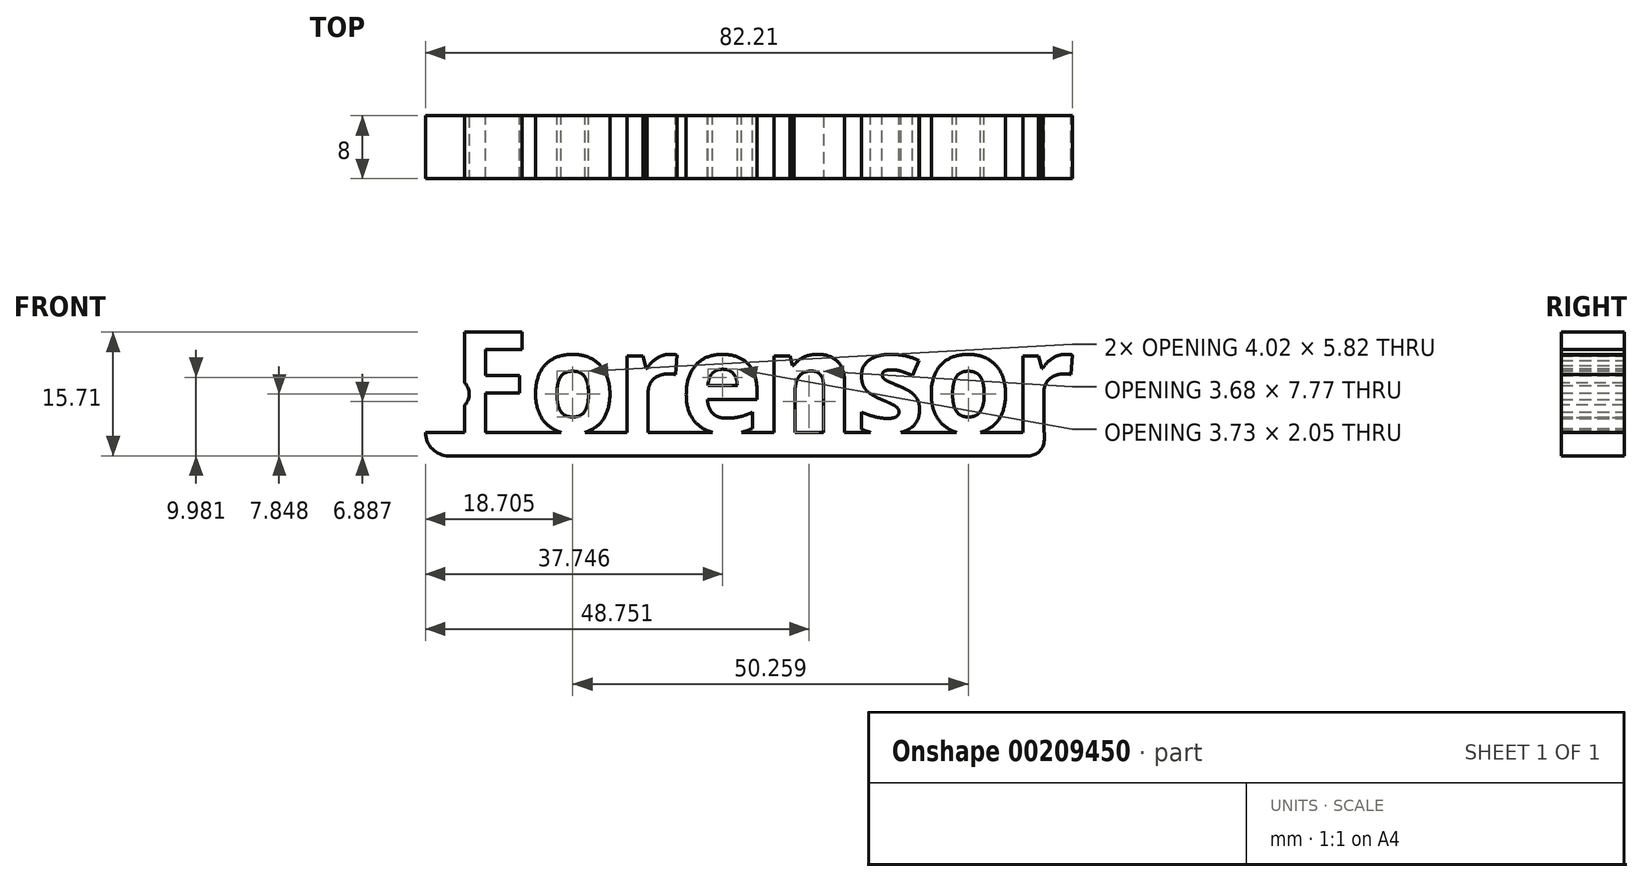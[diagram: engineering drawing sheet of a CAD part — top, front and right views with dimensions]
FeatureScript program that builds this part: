
annotation { "Feature Type Name" : "Feature", "Feature Type Description" : "" }
export const myFeature = defineFeature(function(context is Context, id is Id, definition is map)
    precondition{}
    {
        {
            var Q0;
            Q0=qCreatedBy(makeId("Top.planeOp"),FACE);
            var sketch = newSketch(context, id + "F0", { "sketchPlane" : qUnion([Q0])});
            skLineSegment(sketch, "E0.bottom", {"start": v(36.8, -4) * mm, "end": v(-36.8, -4) * mm});
            skLineSegment(sketch, "E0.top", {"start": v(36.8, 4) * mm, "end": v(-36.8, 4) * mm});
            skLineSegment(sketch, "E0.left", {"start": v(36.8, -4) * mm, "end": v(36.8, 4) * mm});
            skLineSegment(sketch, "E0.right", {"start": v(-36.8, -4) * mm, "end": v(-36.8, 4) * mm});
            skPoint(sketch, "E0.middle", {"position": v(0, 0) * mm});
            skSolve(sketch);
        }
        {
            var Q0;
            Q0=makeQuery(id+"F0.imprint","IMPRINT",FACE,{"disambiguationData":[TD([[makeQuery(id+"F0.imprint","IMPRINT",EDGE,{"derivedFrom":sQuery(id+"F0.wireOp",EDGE,"E0.bottom")}),-1.0]])]});
            extrude(context, id + "F1", {"entities" : qUnion([Q0]), "depth" : 2 * mm, "hasSecondDirection" : true, "secondDirectionOppositeDirection" : true, "secondDirectionDepth" : 1 * mm});
        }
        {
            var Q0;
            Q0=qCreatedBy(makeId("Front.planeOp"),FACE);
            var sketch = newSketch(context, id + "F2", { "sketchPlane" : qUnion([Q0])});
            skLineSegment(sketch, "E1.bottom", {"start": v(-40, 0) * mm, "end": v(40, 0) * mm, "construction": true});
            skLineSegment(sketch, "E1.top", {"start": v(-40, 1.98) * mm, "end": v(40, 1.98) * mm, "construction": true});
            skLineSegment(sketch, "E1.left", {"start": v(-40, 0) * mm, "end": v(-40, 1.98) * mm, "construction": true});
            skLineSegment(sketch, "E1.right", {"start": v(40, 0) * mm, "end": v(40, 1.98) * mm, "construction": true});
            skText(sketch, "E2", { "text": "Forensor", "fontName": "OpenSans-Bold.ttf"});
            skLineSegment(sketch, "E3", {"start": v(0, 0) * mm, "end": v(0, 20.14) * mm, "construction": true});
            const initialGuessF2  = {"E2": [-0.0384, 0.00198, 1, 0, 0.01284]};
            skSetInitialGuess(sketch, initialGuessF2);
            skSolve(sketch);
        }
        {
            var Q0;
            Q0 = qSketchRegion(id + "F2", true);
            extrude(context, id + "F3", {"entities" : qUnion([Q0]), "operationType" : NewBodyOperationType.ADD, "endBound" : BoundingType.SYMMETRIC, "depth" : 8 * mm});
        }
        {
            var Q0;
            Q0=makeQuery(id+"F3.opExtrude","SWEPT_FACE",FACE,{"disambiguationData":[OSD([sQuery(id+"F2.wireOp",EDGE,"E2.sketch_text.stroke-1")])]});
            var sketch = newSketch(context, id + "F4", { "sketchPlane" : qUnion([Q0])});
            skLineSegment(sketch, "E4.bottom", {"start": v(-4, 14.72) * mm, "end": v(4, 14.72) * mm});
            skLineSegment(sketch, "E4.top", {"start": v(-4, 1.5) * mm, "end": v(4, 1.5) * mm});
            skLineSegment(sketch, "E4.left", {"start": v(-4, 14.72) * mm, "end": v(-4, 1.5) * mm});
            skLineSegment(sketch, "E4.right", {"start": v(4, 14.72) * mm, "end": v(4, 1.5) * mm});
            skSolve(sketch);
        }
        {
            var Q0;
            {var subQ0=sQuery(id+"F4.wireOp",EDGE,"E4.bottom");Q0=makeQuery(id+"F4.imprint","IMPRINT",FACE,{"disambiguationData":[TD([[makeQuery(id+"F4.imprint","IMPRINT",EDGE,{"derivedFrom":subQ0}),1.0]])]});}
            var Q1;
            Q1=makeQuery(id+"F1.opExtrude","SWEPT_FACE",FACE,{"disambiguationData":[OSD([sQuery(id+"F0.wireOp",EDGE,"E0.right")])]});
            extrude(context, id + "F5", {"entities" : qUnion([Q0, Q1]), "operationType" : NewBodyOperationType.ADD, "depth" : 5 * mm});
        }
        {
            var Q0;
            Q0=makeQuery(id+"F5.opExtrude","CAP_EDGE",EDGE,{"disambiguationData":[OSD([sQuery(id+"F4.wireOp",EDGE,"E4.bottom")])],"isStart":false});
            var Q1;
            Q1=makeQuery(id+"F5.opExtrude","CAP_EDGE",EDGE,{"disambiguationData":[OSD([sQuery(id+"F0.wireOp",EDGE,"E0.right")])],"isStart":false});
            fillet(context, id + "F6", {"entities" : qUnion([Q0, Q1]), "radius" : 3 * mm, "tangentPropagation" : true, "allowEdgeOverflow" : false});
        }
        {
            var Q0;
            {var subQ0=sQuery(id+"F0.wireOp",EDGE,"E0.bottom");Q0=makeQuery(id+"F5.boolean.opBoolean","MERGE",FACE,{"derivedFrom":[makeQuery(id+"F3.boolean.opBoolean","MERGE",FACE,{"derivedFrom":[makeQuery(id+"F1.opExtrude","SWEPT_FACE",FACE,{"disambiguationData":[OSD([subQ0])]}),makeQuery(id+"F3.opExtrude","CAP_FACE",FACE,{"disambiguationData":[OSD([sQuery(id+"F2.wireOp",EDGE,"E2.sketch_text.stroke-0"),sQuery(id+"F2.wireOp",EDGE,"E2.sketch_text.stroke-1"),sQuery(id+"F2.wireOp",EDGE,"E2.sketch_text.stroke-2"),sQuery(id+"F2.wireOp",EDGE,"E2.sketch_text.stroke-3"),sQuery(id+"F2.wireOp",EDGE,"E2.sketch_text.stroke-4"),sQuery(id+"F2.wireOp",EDGE,"E2.sketch_text.stroke-5"),sQuery(id+"F2.wireOp",EDGE,"E2.sketch_text.stroke-6"),sQuery(id+"F2.wireOp",EDGE,"E2.sketch_text.stroke-7"),sQuery(id+"F2.wireOp",EDGE,"E2.sketch_text.stroke-8"),sQuery(id+"F2.wireOp",EDGE,"E2.sketch_text.stroke-9")])],"isStart":false}),makeQuery(id+"F3.opExtrude","CAP_FACE",FACE,{"disambiguationData":[OSD([sQuery(id+"F2.wireOp",EDGE,"E2.sketch_text.stroke-10"),sQuery(id+"F2.wireOp",EDGE,"E2.sketch_text.stroke-11"),sQuery(id+"F2.wireOp",EDGE,"E2.sketch_text.stroke-12"),sQuery(id+"F2.wireOp",EDGE,"E2.sketch_text.stroke-13"),sQuery(id+"F2.wireOp",EDGE,"E2.sketch_text.stroke-14"),sQuery(id+"F2.wireOp",EDGE,"E2.sketch_text.stroke-15"),sQuery(id+"F2.wireOp",EDGE,"E2.sketch_text.stroke-16"),sQuery(id+"F2.wireOp",EDGE,"E2.sketch_text.stroke-17"),sQuery(id+"F2.wireOp",EDGE,"E2.sketch_text.stroke-18"),sQuery(id+"F2.wireOp",EDGE,"E2.sketch_text.stroke-19"),sQuery(id+"F2.wireOp",EDGE,"E2.sketch_text.stroke-20"),sQuery(id+"F2.wireOp",EDGE,"E2.sketch_text.stroke-21"),sQuery(id+"F2.wireOp",EDGE,"E2.sketch_text.stroke-22"),sQuery(id+"F2.wireOp",EDGE,"E2.sketch_text.stroke-23"),sQuery(id+"F2.wireOp",EDGE,"E2.sketch_text.stroke-24"),sQuery(id+"F2.wireOp",EDGE,"E2.sketch_text.stroke-25"),sQuery(id+"F2.wireOp",EDGE,"E2.sketch_text.stroke-26"),sQuery(id+"F2.wireOp",EDGE,"E2.sketch_text.stroke-27")])],"isStart":false}),makeQuery(id+"F3.opExtrude","CAP_FACE",FACE,{"disambiguationData":[OSD([sQuery(id+"F2.wireOp",EDGE,"E2.sketch_text.stroke-28"),sQuery(id+"F2.wireOp",EDGE,"E2.sketch_text.stroke-29"),sQuery(id+"F2.wireOp",EDGE,"E2.sketch_text.stroke-30"),sQuery(id+"F2.wireOp",EDGE,"E2.sketch_text.stroke-31"),sQuery(id+"F2.wireOp",EDGE,"E2.sketch_text.stroke-32"),sQuery(id+"F2.wireOp",EDGE,"E2.sketch_text.stroke-33"),sQuery(id+"F2.wireOp",EDGE,"E2.sketch_text.stroke-34"),sQuery(id+"F2.wireOp",EDGE,"E2.sketch_text.stroke-35"),sQuery(id+"F2.wireOp",EDGE,"E2.sketch_text.stroke-36"),sQuery(id+"F2.wireOp",EDGE,"E2.sketch_text.stroke-37"),sQuery(id+"F2.wireOp",EDGE,"E2.sketch_text.stroke-38"),sQuery(id+"F2.wireOp",EDGE,"E2.sketch_text.stroke-39"),sQuery(id+"F2.wireOp",EDGE,"E2.sketch_text.stroke-40")])],"isStart":false}),makeQuery(id+"F3.opExtrude","CAP_FACE",FACE,{"disambiguationData":[OSD([sQuery(id+"F2.wireOp",EDGE,"E2.sketch_text.stroke-41"),sQuery(id+"F2.wireOp",EDGE,"E2.sketch_text.stroke-42"),sQuery(id+"F2.wireOp",EDGE,"E2.sketch_text.stroke-43"),sQuery(id+"F2.wireOp",EDGE,"E2.sketch_text.stroke-44"),sQuery(id+"F2.wireOp",EDGE,"E2.sketch_text.stroke-45"),sQuery(id+"F2.wireOp",EDGE,"E2.sketch_text.stroke-46"),sQuery(id+"F2.wireOp",EDGE,"E2.sketch_text.stroke-47"),sQuery(id+"F2.wireOp",EDGE,"E2.sketch_text.stroke-48"),sQuery(id+"F2.wireOp",EDGE,"E2.sketch_text.stroke-49"),sQuery(id+"F2.wireOp",EDGE,"E2.sketch_text.stroke-50"),sQuery(id+"F2.wireOp",EDGE,"E2.sketch_text.stroke-51"),sQuery(id+"F2.wireOp",EDGE,"E2.sketch_text.stroke-52"),sQuery(id+"F2.wireOp",EDGE,"E2.sketch_text.stroke-53"),sQuery(id+"F2.wireOp",EDGE,"E2.sketch_text.stroke-54"),sQuery(id+"F2.wireOp",EDGE,"E2.sketch_text.stroke-55"),sQuery(id+"F2.wireOp",EDGE,"E2.sketch_text.stroke-56"),sQuery(id+"F2.wireOp",EDGE,"E2.sketch_text.stroke-57"),sQuery(id+"F2.wireOp",EDGE,"E2.sketch_text.stroke-58"),sQuery(id+"F2.wireOp",EDGE,"E2.sketch_text.stroke-59"),sQuery(id+"F2.wireOp",EDGE,"E2.sketch_text.stroke-60")])],"isStart":false}),makeQuery(id+"F3.opExtrude","CAP_FACE",FACE,{"disambiguationData":[OSD([sQuery(id+"F2.wireOp",EDGE,"E2.sketch_text.stroke-61"),sQuery(id+"F2.wireOp",EDGE,"E2.sketch_text.stroke-62"),sQuery(id+"F2.wireOp",EDGE,"E2.sketch_text.stroke-63"),sQuery(id+"F2.wireOp",EDGE,"E2.sketch_text.stroke-64"),sQuery(id+"F2.wireOp",EDGE,"E2.sketch_text.stroke-65"),sQuery(id+"F2.wireOp",EDGE,"E2.sketch_text.stroke-66"),sQuery(id+"F2.wireOp",EDGE,"E2.sketch_text.stroke-67"),sQuery(id+"F2.wireOp",EDGE,"E2.sketch_text.stroke-68"),sQuery(id+"F2.wireOp",EDGE,"E2.sketch_text.stroke-69"),sQuery(id+"F2.wireOp",EDGE,"E2.sketch_text.stroke-70"),sQuery(id+"F2.wireOp",EDGE,"E2.sketch_text.stroke-71"),sQuery(id+"F2.wireOp",EDGE,"E2.sketch_text.stroke-72"),sQuery(id+"F2.wireOp",EDGE,"E2.sketch_text.stroke-73"),sQuery(id+"F2.wireOp",EDGE,"E2.sketch_text.stroke-74"),sQuery(id+"F2.wireOp",EDGE,"E2.sketch_text.stroke-75"),sQuery(id+"F2.wireOp",EDGE,"E2.sketch_text.stroke-76"),sQuery(id+"F2.wireOp",EDGE,"E2.sketch_text.stroke-77")])],"isStart":false}),makeQuery(id+"F3.opExtrude","CAP_FACE",FACE,{"disambiguationData":[OSD([sQuery(id+"F2.wireOp",EDGE,"E2.sketch_text.stroke-78"),sQuery(id+"F2.wireOp",EDGE,"E2.sketch_text.stroke-79"),sQuery(id+"F2.wireOp",EDGE,"E2.sketch_text.stroke-80"),sQuery(id+"F2.wireOp",EDGE,"E2.sketch_text.stroke-81"),sQuery(id+"F2.wireOp",EDGE,"E2.sketch_text.stroke-82"),sQuery(id+"F2.wireOp",EDGE,"E2.sketch_text.stroke-83"),sQuery(id+"F2.wireOp",EDGE,"E2.sketch_text.stroke-84"),sQuery(id+"F2.wireOp",EDGE,"E2.sketch_text.stroke-85"),sQuery(id+"F2.wireOp",EDGE,"E2.sketch_text.stroke-86"),sQuery(id+"F2.wireOp",EDGE,"E2.sketch_text.stroke-87"),sQuery(id+"F2.wireOp",EDGE,"E2.sketch_text.stroke-88"),sQuery(id+"F2.wireOp",EDGE,"E2.sketch_text.stroke-89"),sQuery(id+"F2.wireOp",EDGE,"E2.sketch_text.stroke-90"),sQuery(id+"F2.wireOp",EDGE,"E2.sketch_text.stroke-91"),sQuery(id+"F2.wireOp",EDGE,"E2.sketch_text.stroke-92"),sQuery(id+"F2.wireOp",EDGE,"E2.sketch_text.stroke-93"),sQuery(id+"F2.wireOp",EDGE,"E2.sketch_text.stroke-94"),sQuery(id+"F2.wireOp",EDGE,"E2.sketch_text.stroke-95"),sQuery(id+"F2.wireOp",EDGE,"E2.sketch_text.stroke-96"),sQuery(id+"F2.wireOp",EDGE,"E2.sketch_text.stroke-97"),sQuery(id+"F2.wireOp",EDGE,"E2.sketch_text.stroke-98"),sQuery(id+"F2.wireOp",EDGE,"E2.sketch_text.stroke-99"),sQuery(id+"F2.wireOp",EDGE,"E2.sketch_text.stroke-100"),sQuery(id+"F2.wireOp",EDGE,"E2.sketch_text.stroke-101"),sQuery(id+"F2.wireOp",EDGE,"E2.sketch_text.stroke-102"),sQuery(id+"F2.wireOp",EDGE,"E2.sketch_text.stroke-103")])],"isStart":false}),makeQuery(id+"F3.opExtrude","CAP_FACE",FACE,{"disambiguationData":[OSD([sQuery(id+"F2.wireOp",EDGE,"E2.sketch_text.stroke-104"),sQuery(id+"F2.wireOp",EDGE,"E2.sketch_text.stroke-105"),sQuery(id+"F2.wireOp",EDGE,"E2.sketch_text.stroke-106"),sQuery(id+"F2.wireOp",EDGE,"E2.sketch_text.stroke-107"),sQuery(id+"F2.wireOp",EDGE,"E2.sketch_text.stroke-108"),sQuery(id+"F2.wireOp",EDGE,"E2.sketch_text.stroke-109"),sQuery(id+"F2.wireOp",EDGE,"E2.sketch_text.stroke-110"),sQuery(id+"F2.wireOp",EDGE,"E2.sketch_text.stroke-111"),sQuery(id+"F2.wireOp",EDGE,"E2.sketch_text.stroke-112"),sQuery(id+"F2.wireOp",EDGE,"E2.sketch_text.stroke-113"),sQuery(id+"F2.wireOp",EDGE,"E2.sketch_text.stroke-114"),sQuery(id+"F2.wireOp",EDGE,"E2.sketch_text.stroke-115"),sQuery(id+"F2.wireOp",EDGE,"E2.sketch_text.stroke-116"),sQuery(id+"F2.wireOp",EDGE,"E2.sketch_text.stroke-117"),sQuery(id+"F2.wireOp",EDGE,"E2.sketch_text.stroke-118"),sQuery(id+"F2.wireOp",EDGE,"E2.sketch_text.stroke-119"),sQuery(id+"F2.wireOp",EDGE,"E2.sketch_text.stroke-120"),sQuery(id+"F2.wireOp",EDGE,"E2.sketch_text.stroke-121")])],"isStart":false}),makeQuery(id+"F3.opExtrude","CAP_FACE",FACE,{"disambiguationData":[OSD([sQuery(id+"F2.wireOp",EDGE,"E2.sketch_text.stroke-122"),sQuery(id+"F2.wireOp",EDGE,"E2.sketch_text.stroke-123"),sQuery(id+"F2.wireOp",EDGE,"E2.sketch_text.stroke-124"),sQuery(id+"F2.wireOp",EDGE,"E2.sketch_text.stroke-125"),sQuery(id+"F2.wireOp",EDGE,"E2.sketch_text.stroke-126"),sQuery(id+"F2.wireOp",EDGE,"E2.sketch_text.stroke-127"),sQuery(id+"F2.wireOp",EDGE,"E2.sketch_text.stroke-128"),sQuery(id+"F2.wireOp",EDGE,"E2.sketch_text.stroke-129"),sQuery(id+"F2.wireOp",EDGE,"E2.sketch_text.stroke-130"),sQuery(id+"F2.wireOp",EDGE,"E2.sketch_text.stroke-131"),sQuery(id+"F2.wireOp",EDGE,"E2.sketch_text.stroke-132"),sQuery(id+"F2.wireOp",EDGE,"E2.sketch_text.stroke-133"),sQuery(id+"F2.wireOp",EDGE,"E2.sketch_text.stroke-134")])],"isStart":false})]}),makeQuery(id+"F5.opExtrude","SWEPT_FACE",FACE,{"disambiguationData":[OSD([subQ0,sQuery(id+"F0.wireOp",EDGE,"E0.right")])]}),makeQuery(id+"F5.opExtrude","SWEPT_FACE",FACE,{"disambiguationData":[OSD([sQuery(id+"F4.wireOp",EDGE,"E4.right")])]})]});}
            var sketch = newSketch(context, id + "F7", { "sketchPlane" : qUnion([Q0])});
            skCircle(sketch, "E5", {"center": v(-38.23, 6.86) * mm, "radius": 2 * mm});
            skLineSegment(sketch, "E6", {"start": v(-34.14, 10.86) * mm, "end": v(-41.8, 10.86) * mm, "construction": true});
            skLineSegment(sketch, "E7", {"start": v(-38.22, -1) * mm, "end": v(-38.22, 14.72) * mm, "construction": true});
            skLineSegment(sketch, "E8", {"start": v(-38.22, 6.86) * mm, "end": v(-34.87, 6.86) * mm, "construction": true});
            skSolve(sketch);
        }
        {
            var Q0;
            Q0=makeQuery(id+"F7.imprint","IMPRINT",FACE,{"disambiguationData":[TD([[makeQuery(id+"F7.imprint","IMPRINT",EDGE,{"derivedFrom":sQuery(id+"F7.wireOp",EDGE,"E5")}),1.0]])]});
            extrude(context, id + "F8", {"entities" : qUnion([Q0]), "operationType" : NewBodyOperationType.REMOVE, "oppositeDirection" : true, "depth" : 8 * mm});
        }
        {
            var Q0;
            Q0=makeQuery(id+"F1.opExtrude","CAP_EDGE",EDGE,{"disambiguationData":[OSD([sQuery(id+"F0.wireOp",EDGE,"E0.left")])],"isStart":true});
            fillet(context, id + "F9", {"entities" : qUnion([Q0]), "radius" : 2 * mm, "tangentPropagation" : true, "allowEdgeOverflow" : false});
        }
    });
